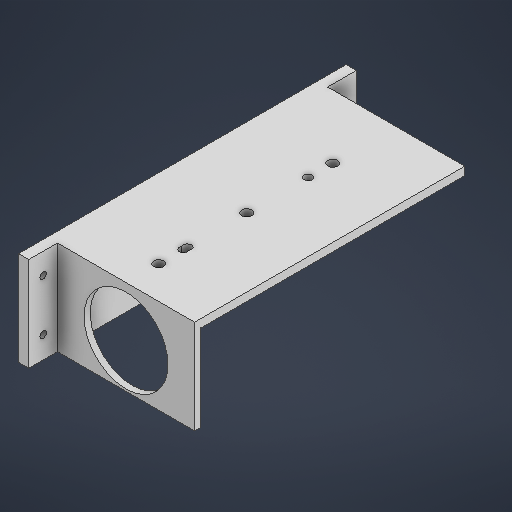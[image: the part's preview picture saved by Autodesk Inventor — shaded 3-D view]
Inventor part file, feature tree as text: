
AUTODESK INVENTOR PART (.ipt)
format: ipt  version: 2025 (Build 290162000, 162)  size: 340,992 bytes
history: native  units: in
note: dims shown in document units (in); Inventor stores cm internally (conversion verified against a paired STEP export)
features: sketch x14, extrude x11, hole x7
ambient origin geometry x8: Origin, YZ Plane, XZ Plane, XY Plane, X Axis, Y Axis, Z Axis, Center Point
bodies: Solid1 (feature_tree)
feature tree (32):
  extrude  "Extrusion1"  Depth=5.0787in
  sketch  "Sketch2"  dims[d2=0.1181in d3=0.0in d4=0.2362in]
  hole  "Hole1"  [1 undecoded]
  hole  "Hole2"  [1 undecoded]
  hole  "Hole3"  [1 undecoded]
  extrude  "Extrusion2"  Depth=2.3622in
  extrude  "Extrusion3"  Depth=0.1181in TaperAngle=0.0deg
  extrude  "Extrusion4"  Depth=0.1181in TaperAngle=0.0deg
  extrude  "Extrusion5"  Depth=0.9252in
  extrude  "Extrusion6"  Depth=0.1969in TaperAngle=0.0deg
  extrude  "Extrusion7"  Depth=0.1969in TaperAngle=0.0deg
  extrude  "Extrusion8"  Depth=0.1969in
  sketch  "Sketch10"  dims[d37=0.1181in d38=1.7717in d39=0.0in]
  hole  "Hole4"  [1 undecoded]
  extrude  "Extrusion10"  Depth=0.1575in
  hole  "Hole5"  [1 undecoded]
  hole  "Hole6"  [1 undecoded]
  hole  "Hole7"  [1 undecoded]
  extrude  "Extrusion11"  Depth=0.0787in
  extrude  "Extrusion12"  Depth=0.1575in
  sketch  "Sketch1"  dims[d0=2.6378in d1=5.0787in]
  sketch  "Sketch3"  dims[d7=0.1575in d8=0.2362in]
  sketch  "Sketch4"  dims[d9=0.5118in d10=2.2047in]
  sketch  "Sketch5"  dims[d11=1.0236in d12=2.3622in]
  sketch  "Sketch6"  dims[d13=3.3465in]
  sketch  "Sketch7"  dims[d14=0.1936in d15=0.4724in d16=0.1575in d17=0.0787in d18=90.0deg d19=0.6732in d20=0.0in]
  sketch  "Sketch8"  dims[d21=0.1575in d22=0.4724in d23=0.1575in d24=0.0787in d25=90.0deg d26=0.6732in d27=0.0in]
  sketch  "Sketch9"  dims[d28=0.196in d29=0.5in d30=0.1575in d31=0.0787in d32=90.0deg d33=0.75in d34=0.0in d35=0.1181in d36=0.0in]
  sketch  "Sketch11"  dims[d40=1.6142in d41=0.9252in]
  sketch  "Sketch12"  dims[d42=1.7717in d43=0.0in d44=0.1969in d45=0.0in]
  sketch  "Sketch13"  dims[d46=0.1969in d47=1.7717in d48=0.0in]
  sketch  "Sketch14"  dims[d49=0.5512in d50=0.0in d51=0.1969in d52=0.5512in d53=0.0in d56=0.1575in d57=0.1575in d58=0.5807in d59=0.2756in d60=0.9843in d61=0.1276in d62=0.3937in d63=0.1575in d64=0.0787in d65=90.0deg d66=0.3937in d67=0.8108in d68=0.1575in d69=0.5807in d70=0.2756in d71=0.2756in d72=0.9843in d73=5.0787in d74=0.1575in d75=1.7717in d76=0.0in d77=0.1936in d78=0.4724in d79=0.1575in d80=0.0787in d81=90.0deg d82=0.315in d83=0.8108in d84=0.196in d85=0.5in d86=0.1575in d87=0.0787in d88=90.0deg d89=0.315in d90=0.8108in d91=0.1575in d92=0.5in d93=0.1575in d94=0.0787in d95=90.0deg d96=0.315in d97=0.8108in d98=0.3937in d99=0.0in d100=0.0787in d101=0.0in]
note: 7 required parameter values undecoded (feature->parameter linkage not recoverable at this tier; creation-order binding heuristic only, values carry confidence <= 0.55)
